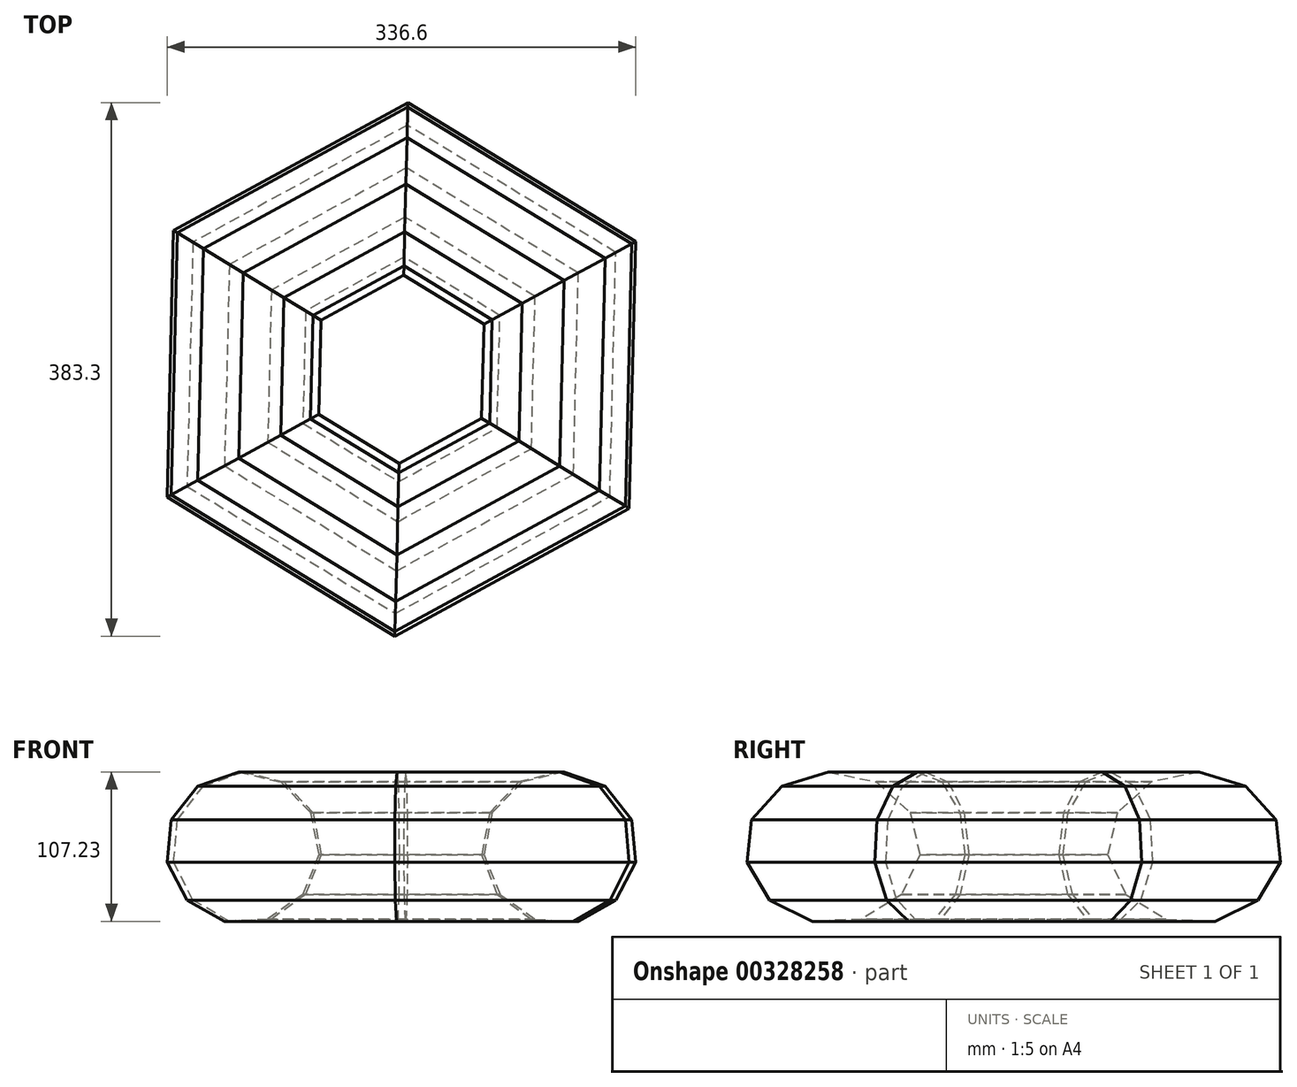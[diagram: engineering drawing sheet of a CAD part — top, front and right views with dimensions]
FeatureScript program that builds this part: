
annotation { "Feature Type Name" : "Feature", "Feature Type Description" : "" }
export const myFeature = defineFeature(function(context is Context, id is Id, definition is map)
    precondition{}
    {
        {
            var Q0;
            Q0=qCreatedBy(makeId("Front.planeOp"),FACE);
            var sketch = newSketch(context, id + "F0", { "sketchPlane" : qUnion([Q0])});
            skCircle(sketch, "E0.cCircle", {"center": v(0, 0) * mm, "radius": 52.2 * mm, "construction": true});
            skLineSegment(sketch, "E0.0", {"start": v(17.92, -51.36) * mm, "end": v(-12.7, -52.9) * mm});
            skLineSegment(sketch, "E0.1", {"start": v(-12.7, -52.9) * mm, "end": v(-39.28, -37.64) * mm});
            skLineSegment(sketch, "E0.2", {"start": v(-39.28, -37.64) * mm, "end": v(-53.4, -10.43) * mm});
            skLineSegment(sketch, "E0.3", {"start": v(-53.4, -10.43) * mm, "end": v(-50.55, 20.1) * mm});
            skLineSegment(sketch, "E0.4", {"start": v(-50.55, 20.1) * mm, "end": v(-31.67, 44.23) * mm});
            skLineSegment(sketch, "E0.5", {"start": v(-31.67, 44.23) * mm, "end": v(-2.72, 54.33) * mm});
            skLineSegment(sketch, "E0.6", {"start": v(-2.72, 54.33) * mm, "end": v(27.08, 47.18) * mm});
            skLineSegment(sketch, "E0.7", {"start": v(27.08, 47.18) * mm, "end": v(48.29, 25.05) * mm});
            skLineSegment(sketch, "E0.8", {"start": v(48.29, 25.05) * mm, "end": v(54.17, -5.04) * mm});
            skLineSegment(sketch, "E0.9", {"start": v(54.17, -5.04) * mm, "end": v(42.84, -33.52) * mm});
            skLineSegment(sketch, "E0.10", {"start": v(42.84, -33.52) * mm, "end": v(17.92, -51.36) * mm});
            skPoint(sketch, "E0.0.midPoint", {"position": v(2.61, -52.13) * mm});
            skSolve(sketch);
        }
        {
            var Q0;
            Q0=qCreatedBy(makeId("Top.planeOp"),FACE);
            var sketch = newSketch(context, id + "F1", { "sketchPlane" : qUnion([Q0])});
            skCircle(sketch, "E1.cCircle", {"center": v(112.68, 0) * mm, "radius": 56.4 * mm, "construction": true});
            skLineSegment(sketch, "E1.0", {"start": v(57.08, 33.92) * mm, "end": v(114.26, 65.1) * mm});
            skLineSegment(sketch, "E1.1", {"start": v(114.26, 65.1) * mm, "end": v(169.86, 31.19) * mm});
            skLineSegment(sketch, "E1.2", {"start": v(169.86, 31.19) * mm, "end": v(168.28, -33.92) * mm});
            skLineSegment(sketch, "E1.3", {"start": v(168.28, -33.92) * mm, "end": v(111.1, -65.1) * mm});
            skLineSegment(sketch, "E1.4", {"start": v(111.1, -65.1) * mm, "end": v(55.5, -31.19) * mm});
            skLineSegment(sketch, "E1.5", {"start": v(55.5, -31.19) * mm, "end": v(57.08, 33.92) * mm});
            skPoint(sketch, "E1.0.midPoint", {"position": v(85.67, 49.52) * mm});
            skCircle(sketch, "E2", {"center": v(112.68, 0) * mm, "radius": 55.15 * mm});
            skSolve(sketch);
        }
        {
            var Q0;
            Q0=makeQuery(id+"F0.imprint","IMPRINT",FACE,{"disambiguationData":[TD([[makeQuery(id+"F0.imprint","IMPRINT",EDGE,{"derivedFrom":sQuery(id+"F0.wireOp",EDGE,"E0.0")}),-1.0]])]});
            var Q1;
            Q1=sQuery(id+"F1.wireOp",EDGE,"E1.4");
            var Q2;
            Q2=sQuery(id+"F1.wireOp",EDGE,"E1.3");
            var Q3;
            Q3=sQuery(id+"F1.wireOp",EDGE,"E1.2");
            var Q4;
            Q4=sQuery(id+"F1.wireOp",EDGE,"E1.1");
            var Q5;
            Q5=sQuery(id+"F1.wireOp",EDGE,"E1.0");
            var Q6;
            Q6=sQuery(id+"F1.wireOp",EDGE,"E1.5");
            sweep(context, id + "F2", {"profiles" : qUnion([Q0]), "path" : qUnion([Q1, Q2, Q3, Q4, Q5, Q6])});
        }
    });
